# Revit family: Electronics_Security-Cameras-Accessories_Traka-ASSA-ABLOY_Key-Cabinet-V-Series-Touch
name_source: partatom
category: Electrical Equipment
revit_build: Autodesk Revit 2015 (Build: 20140606_1530(x64)
units: mm (PartAtom-declared; Revit-internal decimal feet)

## types (1)
- Key Cabinet V-Series Touch
    BIMobject category = Security, Cameras & Accessories
    BIMobject category code = electronics-security
    BIMobject main category = Electronics
    BIMobject main category code = electronics
    Brand url = http://www.traka.com
    Default Elevation = 1219 mm
    Design country = United Kingdom
    Edition number = 1
    IFC Classification = Furnishing Element
    Manufacturer = Traka ASSA ABLOY
    Manufacturer country = United Kingdom
    Manufacturer name = Traka ASSA ABLOY
    Masterformat 2014 Code = 08 79 13
    Masterformat 2014 Description = Key Storage Equipment
    Material main = Steel
    NBS Reference Code = 75-40-02
    NBS Reference Description = Access Control Systems
    OmniClass Code = 23-21 35 21 23
    OmniClass Description = Key Security Cabinets
    Product Guid = 3239dad4-e602-4430-ae33-f984318e03ab
    Product SKU = v-series-touch
    Product data url = https://bimobject.com
    Product family = Key management systems
    Product group = V-Series Touch
    Product name = Key Cabinet V-Series Touch
    Product url = https://www.traka.com
    QR code = http://bimobject.com
    Technical description = https://www.traka.com
    UNSPSC Code = 46171509
    Uniclass 1.4 Code = JW40
    Uniclass 1.4 Description = Access control systems
    Uniclass 2.0 Code = SS-75-40-02
    Uniclass 2.0 Description = Access Control Systems
    Uniclass 2015 Code = Pr_80_77_28_60
    Uniclass 2015 Name = Padlock and key cabinets
    Uniformat II Code = D5030
    Uniformat II Description = Communications & Security

## geometry (parser evidence)
native form markers: Sweep x2
no freeform markers — native parametric forms only
